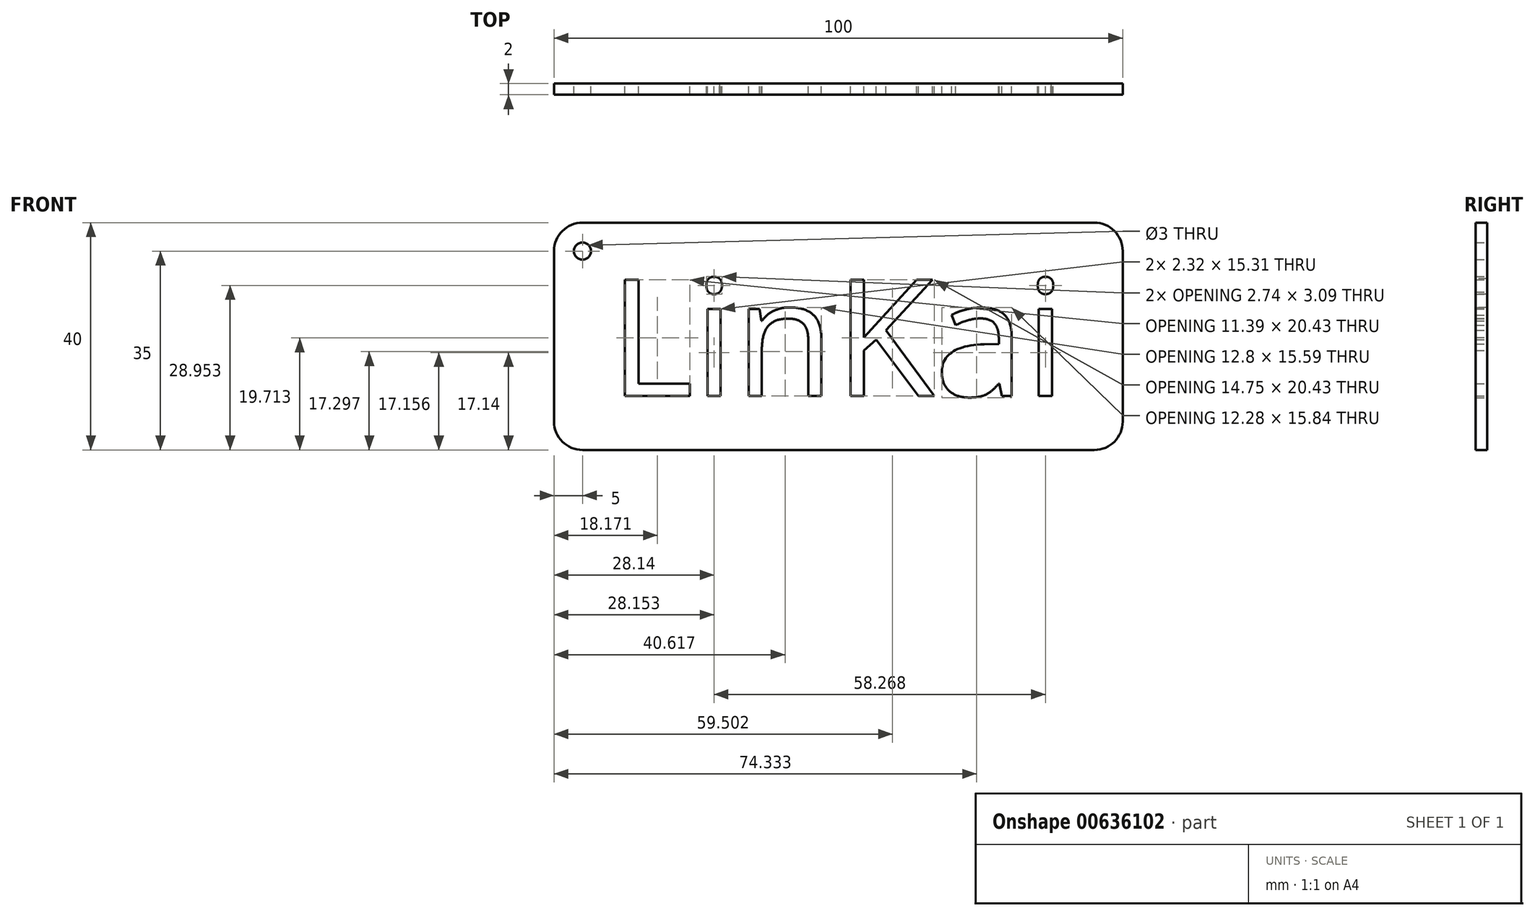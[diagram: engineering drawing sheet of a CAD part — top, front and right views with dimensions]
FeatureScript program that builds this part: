
annotation { "Feature Type Name" : "Feature", "Feature Type Description" : "" }
export const myFeature = defineFeature(function(context is Context, id is Id, definition is map)
    precondition{}
    {
        {
            var Q0;
            Q0=qCreatedBy(makeId("Front.planeOp"),FACE);
            var sketch = newSketch(context, id + "F0", { "sketchPlane" : qUnion([Q0])});
            skLineSegment(sketch, "E0.bottom", {"start": v(5, 0) * mm, "end": v(95, 0) * mm});
            skLineSegment(sketch, "E0.top", {"start": v(5, 40) * mm, "end": v(95, 40) * mm});
            skLineSegment(sketch, "E0.left", {"start": v(0, 5) * mm, "end": v(0, 35) * mm});
            skLineSegment(sketch, "E0.right", {"start": v(100, 5) * mm, "end": v(100, 35) * mm});
            skPoint(sketch, "E1.visualSharp", {"position": v(0, 40) * mm});
            skArc(sketch, "E1.filletArc", {"start": v(5, 40) * mm, "mid": v(1.46, 38.54) * mm, "end": v(0, 35) * mm});
            skPoint(sketch, "E2.visualSharp", {"position": v(0, 0) * mm});
            skArc(sketch, "E2.filletArc", {"start": v(0, 5) * mm, "mid": v(1.46, 1.46) * mm, "end": v(5, 0) * mm});
            skPoint(sketch, "E3.visualSharp", {"position": v(100, 0) * mm});
            skArc(sketch, "E3.filletArc", {"start": v(95, 0) * mm, "mid": v(98.54, 1.46) * mm, "end": v(100, 5) * mm});
            skPoint(sketch, "E4.visualSharp", {"position": v(100, 40) * mm});
            skArc(sketch, "E4.filletArc", {"start": v(100, 35) * mm, "mid": v(98.54, 38.54) * mm, "end": v(95, 40) * mm});
            skCircle(sketch, "E5", {"center": v(5, 35) * mm, "radius": 1.5 * mm});
            skText(sketch, "E6", { "text": "LinKai\n", "fontName": "OpenSans-Regular.ttf"});
            const initialGuessF0  = {"E6": [0.00967, 0.0095, 1, 0, 0.0206]};
            skSetInitialGuess(sketch, initialGuessF0);
            skSolve(sketch);
        }
        {
            var Q0;
            Q0 = qSketchRegion(id + "F0", true);
            extrude(context, id + "F1", {"entities" : qUnion([Q0]), "depth" : 2 * mm, "offsetDistance" : 25 * mm});
        }
    });
